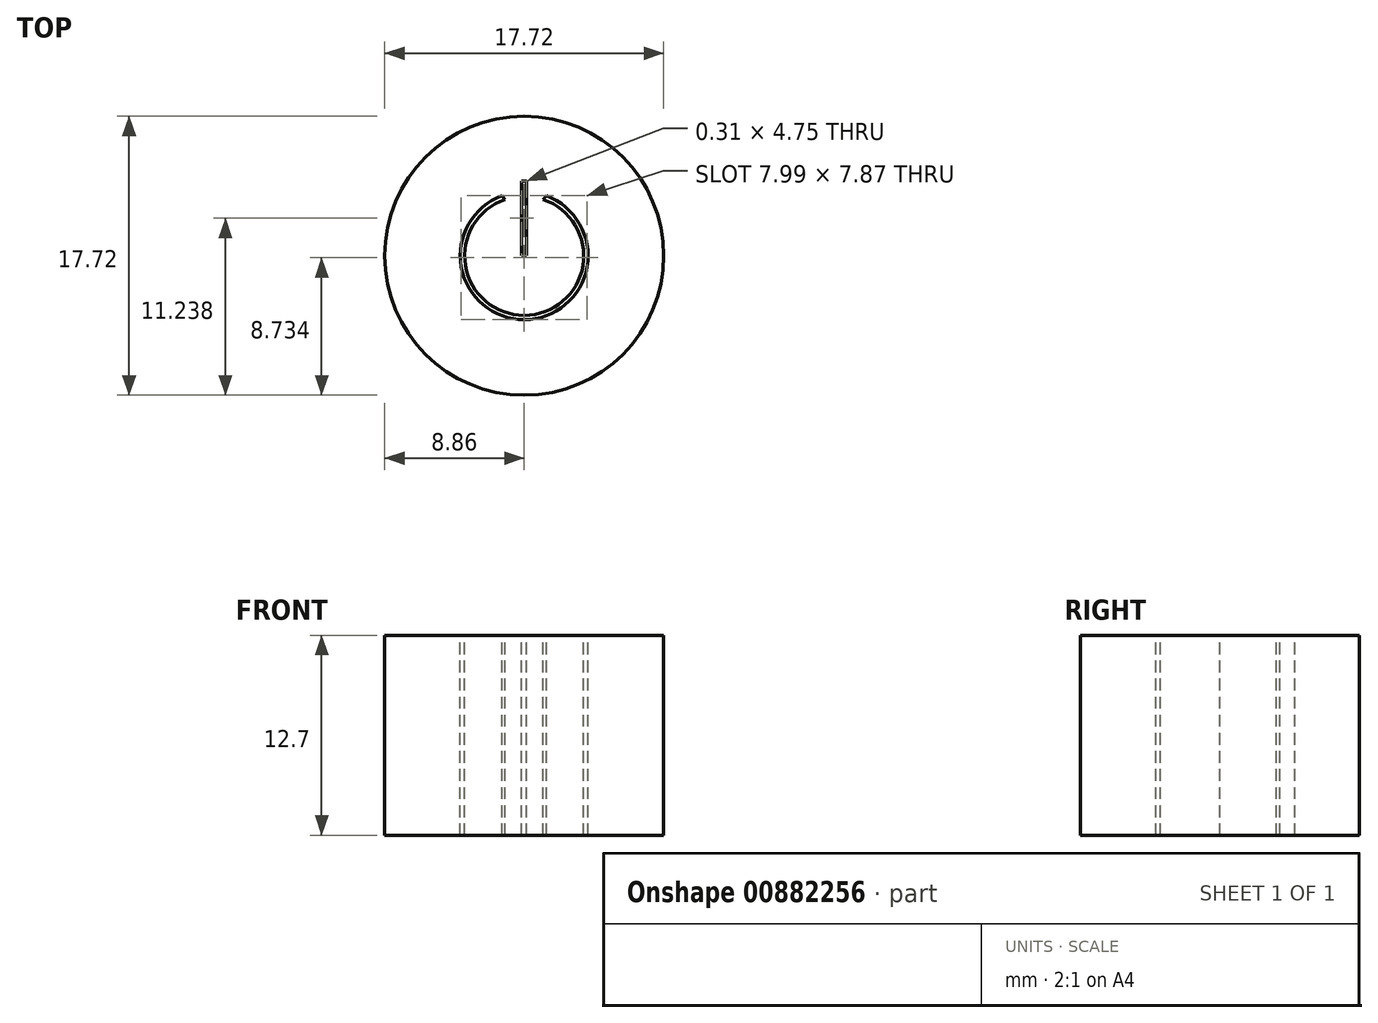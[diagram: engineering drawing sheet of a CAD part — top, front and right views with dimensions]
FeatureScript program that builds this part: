
annotation { "Feature Type Name" : "Feature", "Feature Type Description" : "" }
export const myFeature = defineFeature(function(context is Context, id is Id, definition is map)
    precondition{}
    {
        {
            var Q0;
            Q0=qCreatedBy(makeId("Top.planeOp"),FACE);
            var sketch = newSketch(context, id + "F0", { "sketchPlane" : qUnion([Q0])});
            skCircle(sketch, "E0", {"center": v(0, 0) * mm, "radius": 8.86 * mm});
            skArc(sketch, "E1", {"start": v(-1.2, 3.57) * mm, "mid": v(0, -3.8) * mm, "end": v(1.2, 3.57) * mm});
            skArc(sketch, "E2", {"start": v(-1.4, 3.8) * mm, "mid": v(0, -4.06) * mm, "end": v(1.4, 3.8) * mm});
            skLineSegment(sketch, "E3", {"start": v(-1.4, 3.8) * mm, "end": v(-1.2, 3.57) * mm});
            skLineSegment(sketch, "E4", {"start": v(1.4, 3.8) * mm, "end": v(1.2, 3.57) * mm});
            skLineSegment(sketch, "E5", {"start": v(0, 0) * mm, "end": v(-0.16, 0) * mm});
            skLineSegment(sketch, "E6", {"start": v(0, 0) * mm, "end": v(0.16, 0) * mm});
            skLineSegment(sketch, "E7", {"start": v(-0.16, 0) * mm, "end": v(-0.16, 4.75) * mm});
            skLineSegment(sketch, "E8", {"start": v(0.16, 0) * mm, "end": v(0.16, 4.75) * mm});
            skLineSegment(sketch, "E9", {"start": v(0.16, 4.75) * mm, "end": v(-0.16, 4.75) * mm});
            skSolve(sketch);
        }
        {
            var Q0;
            Q0=makeQuery(id+"F0.imprint","IMPRINT",FACE,{"disambiguationData":[TD([[makeQuery(id+"F0.imprint","IMPRINT",EDGE,{"derivedFrom":sQuery(id+"F0.wireOp",EDGE,"E0")}),1.0]])]});
            extrude(context, id + "F1", {"entities" : qUnion([Q0]), "oppositeDirection" : true, "depth" : 12.7 * mm, "offsetDistance" : 25.4 * mm});
        }
    });
